# Revit family: Domotics-NetworkCabling-GEWISS-CABINETS_FLOOR-MOUNTED_19_24U_D600
name_source: partatom
category: Apparecchi elettrici
units: mm (PartAtom-declared; Revit-internal decimal feet)

## family parameters
Condiviso = No
Host = Superficie
Mantenere orientamento annotazione = Sì
Punto di calcolo locali = Sì
Quota connettore circolare = Usa diametro
Taglio con vuoti quando caricato = No
Tipo di parte = Normale

## types (1)
- GW38451 - FLOOR RACK CABINET 19 24U 600x600MM
    Cabling unity = 24 U
    Catalogue = DOMOTICS
    Category = 19â€ floor-standing cabinet
    Colour = Grey (RAL 7035)
    Depth (mm) = 600 mm
    Descrizione = FLOOR RACK CABINET 19 24U 600x600MM
    Door opening = 135°
    Electrocod = 3752
    Finishing = Textured
    IDF = db74b7e4-7c5a-4a63-b77e-c6ea9bb9c82a
    IDT = 053d00158162476f8ef6cae597f3a83f
    IP degree = IP20
    Immagine tipo = C.jpg
    Material = Steel
    Modello = GW38451
    No. uprights = 2
    Outer dim. LxHxD (mm) = 600x1185x600
    Produttore = GEWISS S.p.A.
    Prospetto di default = 1219 mm
    SEO = Cabinet
    Static load capacity = 1000KG
    Technical sheet = https://www.gewiss.com
    Type of door = Reversible
    URL = https://www.gewiss.com
    Version file RFA = 21.2
    barra din = Sì

## geometry (parser evidence)
native form markers: Sweep x3
no freeform markers — native parametric forms only
